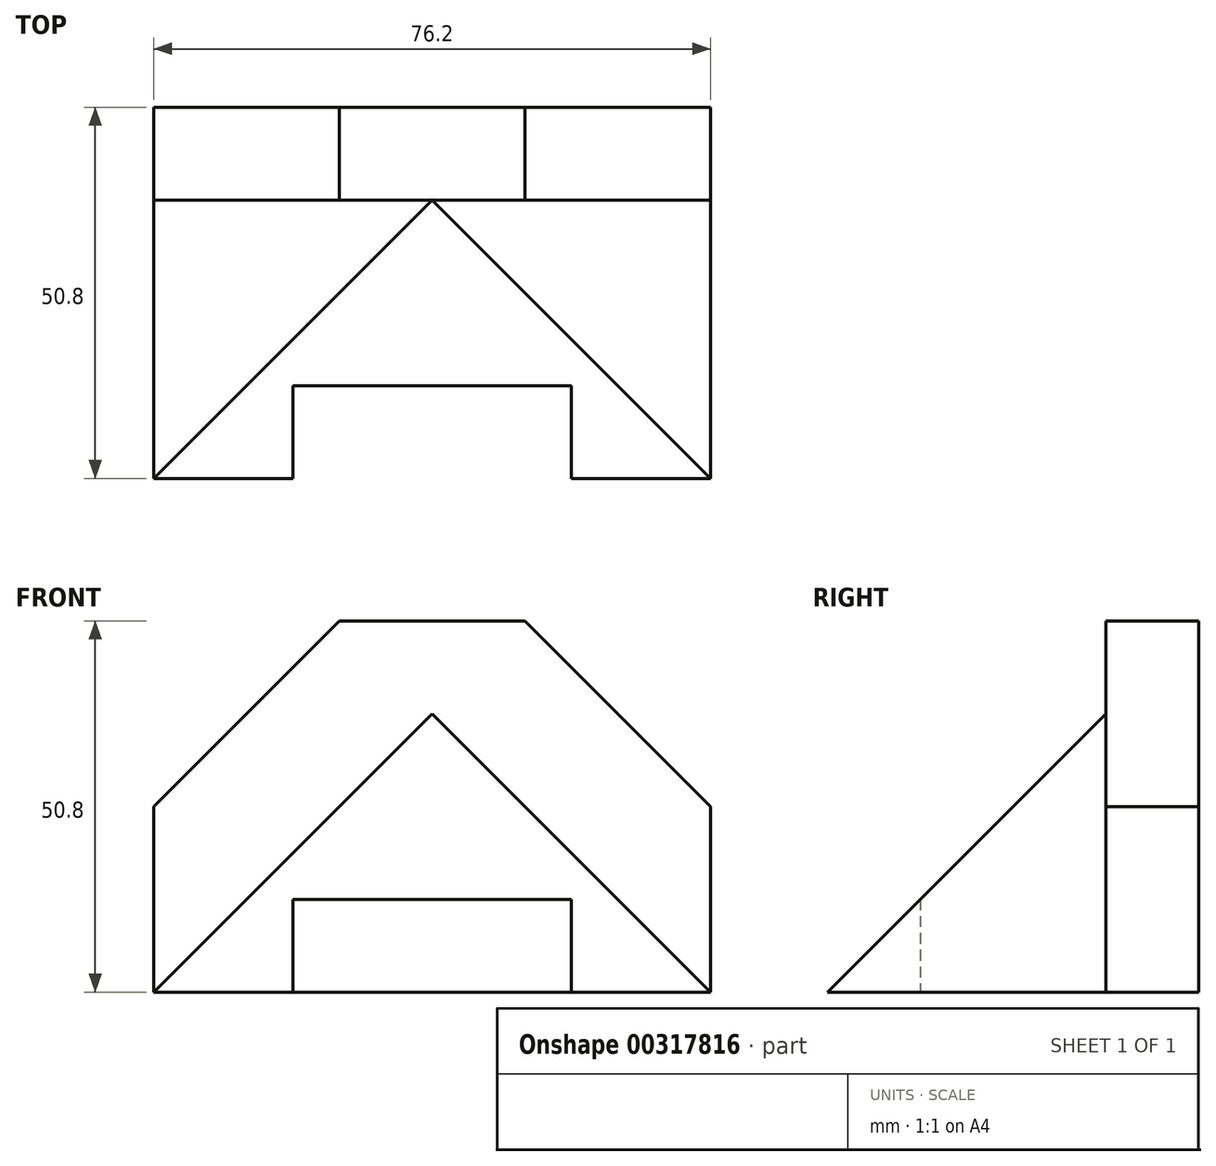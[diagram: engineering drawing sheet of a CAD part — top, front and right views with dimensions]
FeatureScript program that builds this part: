
annotation { "Feature Type Name" : "Feature", "Feature Type Description" : "" }
export const myFeature = defineFeature(function(context is Context, id is Id, definition is map)
    precondition{}
    {
        {
            var Q0;
            Q0=qCreatedBy(makeId("Front.planeOp"),FACE);
            var sketch = newSketch(context, id + "F0", { "sketchPlane" : qUnion([Q0])});
            skLineSegment(sketch, "E0", {"start": v(-38.1, 0) * mm, "end": v(-38.1, 25.4) * mm});
            skLineSegment(sketch, "E1", {"start": v(-38.1, 25.4) * mm, "end": v(-12.7, 50.8) * mm});
            skLineSegment(sketch, "E2", {"start": v(-12.7, 50.8) * mm, "end": v(12.7, 50.8) * mm});
            skLineSegment(sketch, "E3", {"start": v(12.7, 50.8) * mm, "end": v(38.1, 25.4) * mm});
            skLineSegment(sketch, "E4", {"start": v(38.1, 25.4) * mm, "end": v(38.1, 0) * mm});
            skLineSegment(sketch, "E5", {"start": v(38.1, 0) * mm, "end": v(-38.1, 0) * mm});
            skPoint(sketch, "E6", {"position": v(0, 50.8) * mm});
            skPoint(sketch, "E7", {"position": v(0, 0) * mm});
            skSolve(sketch);
        }
        {
            var Q0;
            Q0 = qSketchRegion(id + "F0", true);
            extrude(context, id + "F1", {"entities" : qUnion([Q0]), "oppositeDirection" : true, "depth" : 12.7 * mm});
        }
        {
            var Q0;
            Q0=makeQuery(id+"F1.opExtrude","CAP_FACE",FACE,{"disambiguationData":[OSD([sQuery(id+"F0.wireOp",EDGE,"E0"),sQuery(id+"F0.wireOp",EDGE,"E1"),sQuery(id+"F0.wireOp",EDGE,"E2"),sQuery(id+"F0.wireOp",EDGE,"E3"),sQuery(id+"F0.wireOp",EDGE,"E4"),sQuery(id+"F0.wireOp",EDGE,"E5")])],"isStart":true});
            var sketch = newSketch(context, id + "F2", { "sketchPlane" : qUnion([Q0])});
            skLineSegment(sketch, "E8", {"start": v(-38.1, 0) * mm, "end": v(0, 38.1) * mm});
            skLineSegment(sketch, "E9", {"start": v(0, 38.1) * mm, "end": v(38.1, 0) * mm});
            skLineSegment(sketch, "E10", {"start": v(38.1, 0) * mm, "end": v(-38.1, 0) * mm});
            skSolve(sketch);
        }
        {
            var Q0;
            Q0 = qSketchRegion(id + "F2", true);
            extrude(context, id + "F3", {"entities" : qUnion([Q0]), "operationType" : NewBodyOperationType.ADD, "depth" : 38.1 * mm});
        }
        {
            var Q0;
            Q0=qCreatedBy(makeId("Right.planeOp"),FACE);
            var sketch = newSketch(context, id + "F4", { "sketchPlane" : qUnion([Q0])});
            skLineSegment(sketch, "E11", {"start": v(-38.1, 0) * mm, "end": v(0, 38.1) * mm});
            skLineSegment(sketch, "E12", {"start": v(0, 38.1) * mm, "end": v(-38.1, 38.1) * mm});
            skLineSegment(sketch, "E13", {"start": v(-38.1, 38.1) * mm, "end": v(-38.1, 0) * mm});
            skSolve(sketch);
        }
        {
            var Q0;
            Q0 = qSketchRegion(id + "F4", true);
            extrude(context, id + "F5", {"entities" : qUnion([Q0]), "operationType" : NewBodyOperationType.REMOVE, "endBound" : BoundingType.SYMMETRIC, "oppositeDirection" : true, "depth" : 76.2 * mm});
        }
        {
            var Q0;
            Q0=makeQuery(id+"F3.boolean.opBoolean","MERGE",FACE,{"derivedFrom":[makeQuery(id+"F1.opExtrude","SWEPT_FACE",FACE,{"disambiguationData":[OSD([sQuery(id+"F0.wireOp",EDGE,"E5")])]}),makeQuery(id+"F3.opExtrude","SWEPT_FACE",FACE,{"disambiguationData":[OSD([sQuery(id+"F2.wireOp",EDGE,"E10")])]})]});
            var sketch = newSketch(context, id + "F6", { "sketchPlane" : qUnion([Q0])});
            skLineSegment(sketch, "E14.bottom", {"start": v(-19.05, 38.1) * mm, "end": v(19.05, 38.1) * mm});
            skLineSegment(sketch, "E14.top", {"start": v(-19.05, 25.4) * mm, "end": v(19.05, 25.4) * mm});
            skLineSegment(sketch, "E14.left", {"start": v(-19.05, 38.1) * mm, "end": v(-19.05, 25.4) * mm});
            skLineSegment(sketch, "E14.right", {"start": v(19.05, 38.1) * mm, "end": v(19.05, 25.4) * mm});
            skPoint(sketch, "E15", {"position": v(0, 38.1) * mm});
            skSolve(sketch);
        }
        {
            var Q0;
            Q0 = qSketchRegion(id + "F6", true);
            extrude(context, id + "F7", {"entities" : qUnion([Q0]), "operationType" : NewBodyOperationType.REMOVE, "endBound" : BoundingType.THROUGH_ALL, "oppositeDirection" : true, "depth" : 25.4 * mm});
        }
    });
